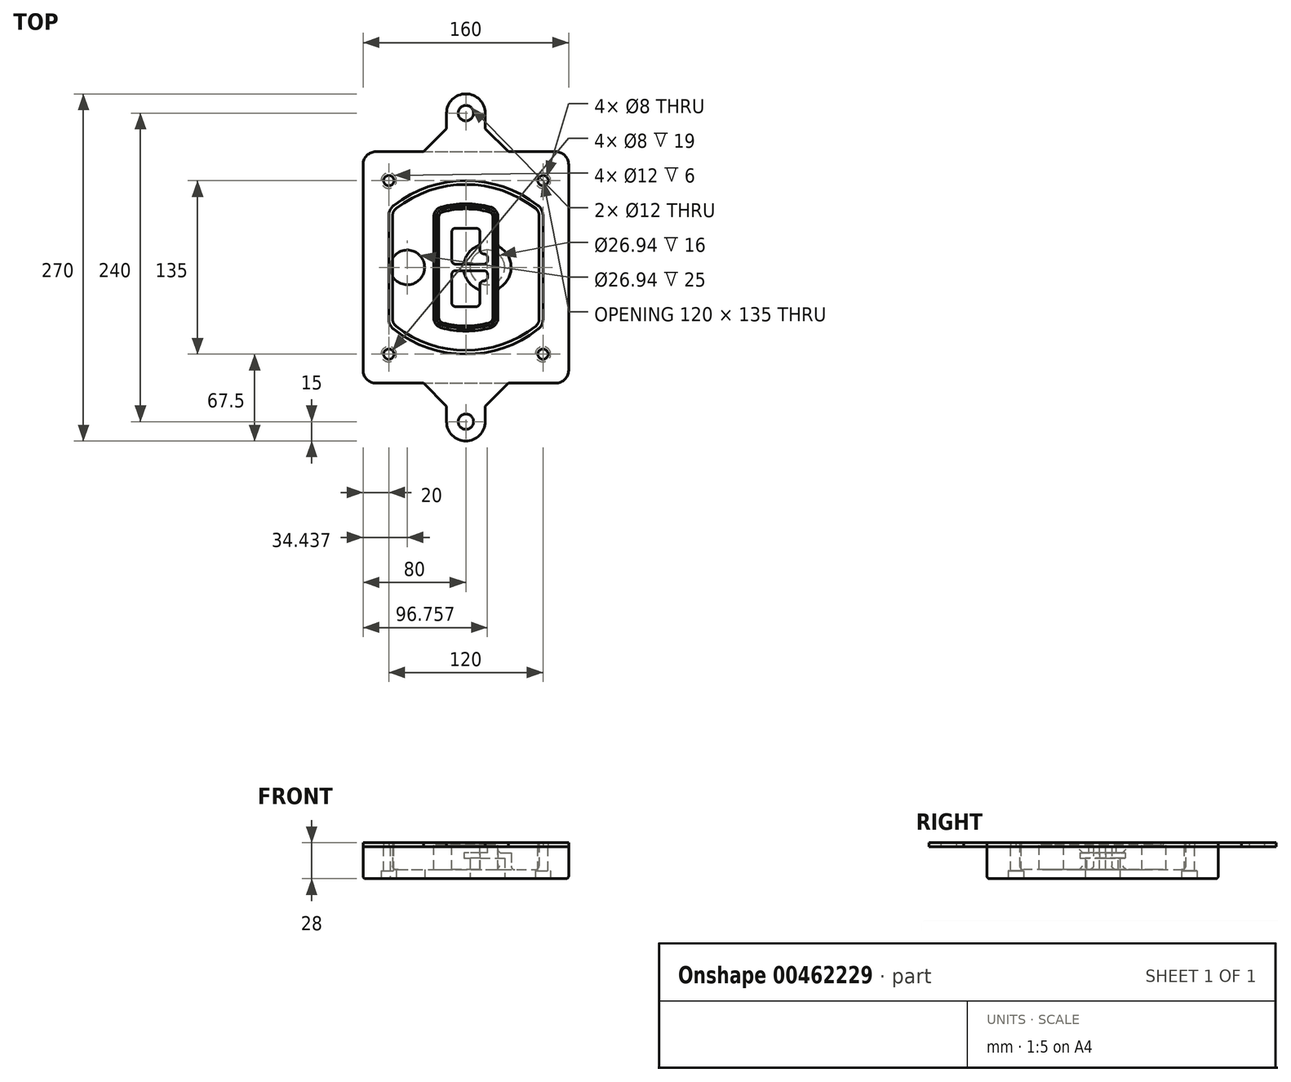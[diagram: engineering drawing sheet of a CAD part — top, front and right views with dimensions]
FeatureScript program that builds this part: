
annotation { "Feature Type Name" : "Feature", "Feature Type Description" : "" }
export const myFeature = defineFeature(function(context is Context, id is Id, definition is map)
    precondition{}
    {
        {
            var Q0;
            Q0=qCreatedBy(makeId("Top.planeOp"),FACE);
            var sketch = newSketch(context, id + "F0", { "sketchPlane" : qUnion([Q0])});
            skPoint(sketch, "E0.rect.middle", {"position": v(0, 0) * mm});
            skLineSegment(sketch, "E1.bottom", {"start": v(-70, -90) * mm, "end": v(70, -90) * mm});
            skLineSegment(sketch, "E1.top", {"start": v(-70, 90) * mm, "end": v(70, 90) * mm});
            skLineSegment(sketch, "E1.left", {"start": v(-80, -80) * mm, "end": v(-80, 80) * mm});
            skLineSegment(sketch, "E1.right", {"start": v(80, -80) * mm, "end": v(80, 80) * mm});
            skLineSegment(sketch, "E2", {"start": v(-80, 90) * mm, "end": v(80, -90) * mm, "construction": true});
            skLineSegment(sketch, "E3", {"start": v(80, 90) * mm, "end": v(-80, -90) * mm, "construction": true});
            skCircle(sketch, "E4", {"center": v(-60, 67.5) * mm, "radius": 4 * mm});
            skCircle(sketch, "E5", {"center": v(60, 67.5) * mm, "radius": 4 * mm});
            skCircle(sketch, "E6", {"center": v(60, -67.5) * mm, "radius": 4 * mm});
            skCircle(sketch, "E7", {"center": v(-60, -67.5) * mm, "radius": 4 * mm});
            skLineSegment(sketch, "E8", {"start": v(-60, 67.5) * mm, "end": v(60, 67.5) * mm, "construction": true});
            skLineSegment(sketch, "E9", {"start": v(60, 67.5) * mm, "end": v(60, -67.5) * mm, "construction": true});
            skLineSegment(sketch, "E10", {"start": v(60, -67.5) * mm, "end": v(-60, -67.5) * mm, "construction": true});
            skLineSegment(sketch, "E11", {"start": v(-60, -67.5) * mm, "end": v(-60, 67.5) * mm, "construction": true});
            skLineSegment(sketch, "E12", {"start": v(-60, 40.3) * mm, "end": v(-60, -40.3) * mm});
            skLineSegment(sketch, "E13", {"start": v(60, 40.3) * mm, "end": v(60, -40.3) * mm});
            skArc(sketch, "E14", {"start": v(56.15, 48.18) * mm, "mid": v(0, 67.5) * mm, "end": v(-56.15, 48.18) * mm});
            skArc(sketch, "E15", {"start": v(-56.15, -48.18) * mm, "mid": v(0, -67.5) * mm, "end": v(56.15, -48.18) * mm});
            skLineSegment(sketch, "E16", {"start": v(-60, 0) * mm, "end": v(60, 0) * mm, "construction": true});
            skPoint(sketch, "E17.visualSharp", {"position": v(-60, -45) * mm});
            skArc(sketch, "E17.filletArc", {"start": v(-60, -40.3) * mm, "mid": v(-58.99, -44.68) * mm, "end": v(-56.15, -48.18) * mm});
            skPoint(sketch, "E18.visualSharp", {"position": v(-60, 45) * mm});
            skArc(sketch, "E18.filletArc", {"start": v(-56.15, 48.18) * mm, "mid": v(-58.99, 44.68) * mm, "end": v(-60, 40.3) * mm});
            skPoint(sketch, "E19.visualSharp", {"position": v(60, 45) * mm});
            skArc(sketch, "E19.filletArc", {"start": v(60, 40.3) * mm, "mid": v(58.99, 44.68) * mm, "end": v(56.15, 48.18) * mm});
            skPoint(sketch, "E20.visualSharp", {"position": v(60, -45) * mm});
            skArc(sketch, "E20.filletArc", {"start": v(56.15, -48.18) * mm, "mid": v(58.99, -44.68) * mm, "end": v(60, -40.3) * mm});
            skPoint(sketch, "E21.visualSharp", {"position": v(-80, 90) * mm});
            skArc(sketch, "E21.filletArc", {"start": v(-70, 90) * mm, "mid": v(-77.07, 87.07) * mm, "end": v(-80, 80) * mm});
            skPoint(sketch, "E22.visualSharp", {"position": v(80, 90) * mm});
            skArc(sketch, "E22.filletArc", {"start": v(80, 80) * mm, "mid": v(77.07, 87.07) * mm, "end": v(70, 90) * mm});
            skPoint(sketch, "E23.visualSharp", {"position": v(80, -90) * mm});
            skArc(sketch, "E23.filletArc", {"start": v(70, -90) * mm, "mid": v(77.07, -87.07) * mm, "end": v(80, -80) * mm});
            skPoint(sketch, "E24.visualSharp", {"position": v(-80, -90) * mm});
            skArc(sketch, "E24.filletArc", {"start": v(-80, -80) * mm, "mid": v(-77.07, -87.07) * mm, "end": v(-70, -90) * mm});
            skArc(sketch, "E25.0", {"start": v(57, 40.3) * mm, "mid": v(56.3, 43.36) * mm, "end": v(54.3, 45.81) * mm});
            skLineSegment(sketch, "E25.1", {"start": v(57, 40.3) * mm, "end": v(57, -40.3) * mm});
            skArc(sketch, "E25.2", {"start": v(54.3, -45.81) * mm, "mid": v(56.3, -43.36) * mm, "end": v(57, -40.3) * mm});
            skArc(sketch, "E25.3", {"start": v(-54.3, -45.81) * mm, "mid": v(0, -64.5) * mm, "end": v(54.3, -45.81) * mm});
            skArc(sketch, "E25.4", {"start": v(-57, -40.3) * mm, "mid": v(-56.3, -43.36) * mm, "end": v(-54.3, -45.81) * mm});
            skArc(sketch, "E25.5", {"start": v(54.3, 45.81) * mm, "mid": v(0, 64.5) * mm, "end": v(-54.3, 45.81) * mm});
            skLineSegment(sketch, "E25.6", {"start": v(-57, 40.3) * mm, "end": v(-57, -40.3) * mm});
            skArc(sketch, "E25.7", {"start": v(-54.3, 45.81) * mm, "mid": v(-56.3, 43.36) * mm, "end": v(-57, 40.3) * mm});
            skArc(sketch, "E26.0", {"start": v(-58.62, 51.33) * mm, "mid": v(-62.58, 46.43) * mm, "end": v(-64, 40.3) * mm});
            skArc(sketch, "E26.1", {"start": v(58.62, 51.33) * mm, "mid": v(0, 71.5) * mm, "end": v(-58.62, 51.33) * mm});
            skArc(sketch, "E26.2", {"start": v(64, 40.3) * mm, "mid": v(62.58, 46.43) * mm, "end": v(58.62, 51.33) * mm});
            skLineSegment(sketch, "E26.3", {"start": v(64, 40.3) * mm, "end": v(64, -40.3) * mm});
            skArc(sketch, "E26.4", {"start": v(58.62, -51.33) * mm, "mid": v(62.58, -46.43) * mm, "end": v(64, -40.3) * mm});
            skLineSegment(sketch, "E26.5", {"start": v(-64, 40.3) * mm, "end": v(-64, -40.3) * mm});
            skArc(sketch, "E26.6", {"start": v(-58.62, -51.33) * mm, "mid": v(0, -71.5) * mm, "end": v(58.62, -51.33) * mm});
            skArc(sketch, "E26.7", {"start": v(-64, -40.3) * mm, "mid": v(-62.58, -46.43) * mm, "end": v(-58.62, -51.33) * mm});
            skSolve(sketch);
        }
        {
            var Q0;
            Q0=makeQuery(id+"F0.imprint","IMPRINT",FACE,{"disambiguationData":[TD([[makeQuery(id+"F0.imprint","IMPRINT",EDGE,{"derivedFrom":sQuery(id+"F0.wireOp",EDGE,"E1.bottom")}),1.0]])]});
            var Q1;
            Q1=makeQuery(id+"F0.imprint","IMPRINT",FACE,{"disambiguationData":[TD([[makeQuery(id+"F0.imprint","IMPRINT",EDGE,{"derivedFrom":sQuery(id+"F0.wireOp",EDGE,"E12")}),1.0]])]});
            var Q2;
            Q2=makeQuery(id+"F0.imprint","IMPRINT",FACE,{"disambiguationData":[TD([[makeQuery(id+"F0.imprint","IMPRINT",EDGE,{"derivedFrom":sQuery(id+"F0.wireOp",EDGE,"E25.0")}),1.0]])]});
            var Q3;
            Q3=makeQuery(id+"F0.imprint","IMPRINT",FACE,{"disambiguationData":[TD([[makeQuery(id+"F0.imprint","IMPRINT",EDGE,{"derivedFrom":sQuery(id+"F0.wireOp",EDGE,"E12")}),-1.0]])]});
            extrude(context, id + "F1", {"entities" : qUnion([Q0, Q1, Q2, Q3]), "oppositeDirection" : true, "depth" : 25 * mm});
        }
        {
            var Q0;
            Q0=makeQuery(id+"F0.imprint","IMPRINT",FACE,{"disambiguationData":[TD([[makeQuery(id+"F0.imprint","IMPRINT",EDGE,{"derivedFrom":sQuery(id+"F0.wireOp",EDGE,"E12")}),1.0]])]});
            extrude(context, id + "F2", {"entities" : qUnion([Q0]), "operationType" : NewBodyOperationType.ADD, "depth" : 3 * mm});
        }
        {
            var Q0;
            Q0=makeQuery(id+"F0.imprint","IMPRINT",FACE,{"disambiguationData":[TD([[makeQuery(id+"F0.imprint","IMPRINT",EDGE,{"derivedFrom":sQuery(id+"F0.wireOp",EDGE,"E25.0")}),1.0]])]});
            extrude(context, id + "F3", {"entities" : qUnion([Q0]), "operationType" : NewBodyOperationType.REMOVE, "oppositeDirection" : true, "depth" : 18 * mm});
        }
        {
            var Q0;
            Q0=makeQuery(id+"F2.opExtrude","CAP_FACE",FACE,{"disambiguationData":[OSD([sQuery(id+"F0.wireOp",EDGE,"E12"),sQuery(id+"F0.wireOp",EDGE,"E13"),sQuery(id+"F0.wireOp",EDGE,"E14"),sQuery(id+"F0.wireOp",EDGE,"E15"),sQuery(id+"F0.wireOp",EDGE,"E17.filletArc"),sQuery(id+"F0.wireOp",EDGE,"E18.filletArc"),sQuery(id+"F0.wireOp",EDGE,"E19.filletArc"),sQuery(id+"F0.wireOp",EDGE,"E20.filletArc"),sQuery(id+"F0.wireOp",EDGE,"E25.0"),sQuery(id+"F0.wireOp",EDGE,"E25.1"),sQuery(id+"F0.wireOp",EDGE,"E25.2"),sQuery(id+"F0.wireOp",EDGE,"E25.3"),sQuery(id+"F0.wireOp",EDGE,"E25.4"),sQuery(id+"F0.wireOp",EDGE,"E25.5"),sQuery(id+"F0.wireOp",EDGE,"E25.6"),sQuery(id+"F0.wireOp",EDGE,"E25.7")])],"isStart":false});
            var sketch = newSketch(context, id + "F4", { "sketchPlane" : qUnion([Q0])});
            skArc(sketch, "E27.0", {"start": v(-19.08, -46.97) * mm, "mid": v(0, -49.5) * mm, "end": v(19.08, -46.97) * mm});
            skArc(sketch, "E28.0", {"start": v(19.08, 46.97) * mm, "mid": v(0, 49.5) * mm, "end": v(-19.08, 46.97) * mm});
            skLineSegment(sketch, "E29", {"start": v(-25, 39.25) * mm, "end": v(-25, -39.25) * mm});
            skLineSegment(sketch, "E30", {"start": v(25, 39.25) * mm, "end": v(25, -39.25) * mm});
            skLineSegment(sketch, "E31", {"start": v(-25, 45.1) * mm, "end": v(25, 45.1) * mm, "construction": true});
            skLineSegment(sketch, "E32", {"start": v(-25, -45.1) * mm, "end": v(25, -45.1) * mm, "construction": true});
            skPoint(sketch, "E33.visualSharp", {"position": v(-25, 45.1) * mm});
            skArc(sketch, "E33.filletArc", {"start": v(-19.08, 46.97) * mm, "mid": v(-23.35, 44.11) * mm, "end": v(-25, 39.25) * mm});
            skPoint(sketch, "E34.visualSharp", {"position": v(25, 45.1) * mm});
            skArc(sketch, "E34.filletArc", {"start": v(25, 39.25) * mm, "mid": v(23.35, 44.11) * mm, "end": v(19.08, 46.97) * mm});
            skPoint(sketch, "E35.visualSharp", {"position": v(25, -45.1) * mm});
            skArc(sketch, "E35.filletArc", {"start": v(19.08, -46.97) * mm, "mid": v(23.35, -44.11) * mm, "end": v(25, -39.25) * mm});
            skPoint(sketch, "E36.visualSharp", {"position": v(-25, -45.1) * mm});
            skArc(sketch, "E36.filletArc", {"start": v(-25, -39.25) * mm, "mid": v(-23.35, -44.11) * mm, "end": v(-19.08, -46.97) * mm});
            skArc(sketch, "E37.0", {"start": v(54.3, 45.81) * mm, "mid": v(0, 64.5) * mm, "end": v(-54.3, 45.81) * mm});
            skArc(sketch, "E37.1", {"start": v(-54.3, 45.81) * mm, "mid": v(-56.3, 43.36) * mm, "end": v(-57, 40.3) * mm});
            skLineSegment(sketch, "E37.2", {"start": v(-57, 40.3) * mm, "end": v(-57, -40.3) * mm});
            skArc(sketch, "E37.3", {"start": v(-57, -40.3) * mm, "mid": v(-56.3, -43.36) * mm, "end": v(-54.3, -45.81) * mm});
            skArc(sketch, "E37.4", {"start": v(-54.3, -45.81) * mm, "mid": v(0, -64.5) * mm, "end": v(54.3, -45.81) * mm});
            skArc(sketch, "E37.5", {"start": v(54.3, -45.81) * mm, "mid": v(56.3, -43.36) * mm, "end": v(57, -40.3) * mm});
            skLineSegment(sketch, "E37.6", {"start": v(57, 40.3) * mm, "end": v(57, -40.3) * mm});
            skArc(sketch, "E37.7", {"start": v(57, 40.3) * mm, "mid": v(56.3, 43.36) * mm, "end": v(54.3, 45.81) * mm});
            skLineSegment(sketch, "E38.0", {"start": v(23, 39.25) * mm, "end": v(23, -39.25) * mm});
            skArc(sketch, "E38.1", {"start": v(18.56, -45.04) * mm, "mid": v(21.76, -42.9) * mm, "end": v(23, -39.25) * mm});
            skArc(sketch, "E38.2", {"start": v(-18.56, -45.04) * mm, "mid": v(0, -47.5) * mm, "end": v(18.56, -45.04) * mm});
            skArc(sketch, "E38.3", {"start": v(-23, -39.25) * mm, "mid": v(-21.76, -42.9) * mm, "end": v(-18.56, -45.04) * mm});
            skLineSegment(sketch, "E38.4", {"start": v(-23, 39.25) * mm, "end": v(-23, -39.25) * mm});
            skArc(sketch, "E38.5", {"start": v(23, 39.25) * mm, "mid": v(21.76, 42.9) * mm, "end": v(18.56, 45.04) * mm});
            skArc(sketch, "E38.6", {"start": v(-18.56, 45.04) * mm, "mid": v(-21.76, 42.9) * mm, "end": v(-23, 39.25) * mm});
            skArc(sketch, "E38.7", {"start": v(18.56, 45.04) * mm, "mid": v(0, 47.5) * mm, "end": v(-18.56, 45.04) * mm});
            skArc(sketch, "E39.0", {"start": v(21, 39.25) * mm, "mid": v(20.18, 41.68) * mm, "end": v(18.04, 43.1) * mm});
            skLineSegment(sketch, "E39.1", {"start": v(21, 39.25) * mm, "end": v(21, -39.25) * mm});
            skArc(sketch, "E39.2", {"start": v(18.04, -43.1) * mm, "mid": v(20.18, -41.68) * mm, "end": v(21, -39.25) * mm});
            skArc(sketch, "E39.3", {"start": v(-18.04, -43.1) * mm, "mid": v(0, -45.5) * mm, "end": v(18.04, -43.1) * mm});
            skArc(sketch, "E39.4", {"start": v(-21, -39.25) * mm, "mid": v(-20.18, -41.68) * mm, "end": v(-18.04, -43.1) * mm});
            skArc(sketch, "E39.5", {"start": v(18.04, 43.1) * mm, "mid": v(0, 45.5) * mm, "end": v(-18.04, 43.1) * mm});
            skLineSegment(sketch, "E39.6", {"start": v(-21, 39.25) * mm, "end": v(-21, -39.25) * mm});
            skArc(sketch, "E39.7", {"start": v(-18.04, 43.1) * mm, "mid": v(-20.18, 41.68) * mm, "end": v(-21, 39.25) * mm});
            skLineSegment(sketch, "E40", {"start": v(-25, 0) * mm, "end": v(25, 0) * mm, "construction": true});
            skLineSegment(sketch, "E41", {"start": v(-11, 5.5) * mm, "end": v(-11, 27.5) * mm});
            skLineSegment(sketch, "E42", {"start": v(-8, 30.5) * mm, "end": v(8, 30.5) * mm});
            skLineSegment(sketch, "E43", {"start": v(11, 27.5) * mm, "end": v(11, 13.5) * mm});
            skLineSegment(sketch, "E44", {"start": v(14, 10.5) * mm, "end": v(14, 10.5) * mm});
            skLineSegment(sketch, "E45", {"start": v(17, 7.5) * mm, "end": v(17, 5.5) * mm});
            skLineSegment(sketch, "E46", {"start": v(14, 2.5) * mm, "end": v(-8, 2.5) * mm});
            skPoint(sketch, "E47.visualSharp", {"position": v(-11, 30.5) * mm});
            skArc(sketch, "E47.filletArc", {"start": v(-8, 30.5) * mm, "mid": v(-10.12, 29.62) * mm, "end": v(-11, 27.5) * mm});
            skPoint(sketch, "E48.visualSharp", {"position": v(11, 30.5) * mm});
            skArc(sketch, "E48.filletArc", {"start": v(11, 27.5) * mm, "mid": v(10.12, 29.62) * mm, "end": v(8, 30.5) * mm});
            skPoint(sketch, "E49.visualSharp", {"position": v(11, 10.5) * mm});
            skArc(sketch, "E49.filletArc", {"start": v(11, 13.5) * mm, "mid": v(11.88, 11.38) * mm, "end": v(14, 10.5) * mm});
            skPoint(sketch, "E50.visualSharp", {"position": v(17, 10.5) * mm});
            skArc(sketch, "E50.filletArc", {"start": v(17, 7.5) * mm, "mid": v(16.12, 9.62) * mm, "end": v(14, 10.5) * mm});
            skPoint(sketch, "E51.visualSharp", {"position": v(17, 2.5) * mm});
            skArc(sketch, "E51.filletArc", {"start": v(14, 2.5) * mm, "mid": v(16.12, 3.38) * mm, "end": v(17, 5.5) * mm});
            skPoint(sketch, "E52.visualSharp", {"position": v(-11, 2.5) * mm});
            skArc(sketch, "E52.filletArc", {"start": v(-11, 5.5) * mm, "mid": v(-10.12, 3.38) * mm, "end": v(-8, 2.5) * mm});
            skLineSegment(sketch, "E53.0.MirrorCS", {"start": v(14, -2.5) * mm, "end": v(-8, -2.5) * mm});
            skArc(sketch, "E54.0.MirrorCS", {"start": v(-11, -5.5) * mm, "mid": v(-10.12, -3.38) * mm, "end": v(-8, -2.5) * mm});
            skLineSegment(sketch, "E55.0.MirrorCS", {"start": v(-11, -5.5) * mm, "end": v(-11, -27.5) * mm});
            skArc(sketch, "E56.0.MirrorCS", {"start": v(-8, -30.5) * mm, "mid": v(-10.12, -29.62) * mm, "end": v(-11, -27.5) * mm});
            skLineSegment(sketch, "E57.0.MirrorCS", {"start": v(-8, -30.5) * mm, "end": v(8, -30.5) * mm});
            skArc(sketch, "E58.0.MirrorCS", {"start": v(11, -27.5) * mm, "mid": v(10.12, -29.62) * mm, "end": v(8, -30.5) * mm});
            skLineSegment(sketch, "E59.0.MirrorCS", {"start": v(11, -27.5) * mm, "end": v(11, -13.5) * mm});
            skArc(sketch, "E60.0.MirrorCS", {"start": v(11, -13.5) * mm, "mid": v(11.88, -11.38) * mm, "end": v(14, -10.5) * mm});
            skArc(sketch, "E61.0.MirrorCS", {"start": v(17, -7.5) * mm, "mid": v(16.12, -9.62) * mm, "end": v(14, -10.5) * mm});
            skLineSegment(sketch, "E62.0.MirrorCS", {"start": v(17, -7.5) * mm, "end": v(17, -5.5) * mm});
            skArc(sketch, "E63.0.MirrorCS", {"start": v(14, -2.5) * mm, "mid": v(16.12, -3.38) * mm, "end": v(17, -5.5) * mm});
            skSolve(sketch);
        }
        {
            var Q0;
            Q0=makeQuery(id+"F4.imprint","IMPRINT",FACE,{"disambiguationData":[TD([[makeQuery(id+"F4.imprint","IMPRINT",EDGE,{"derivedFrom":sQuery(id+"F4.wireOp",EDGE,"E27.0")}),1.0]])]});
            var Q1;
            Q1=makeQuery(id+"F4.imprint","IMPRINT",FACE,{"disambiguationData":[TD([[makeQuery(id+"F4.imprint","IMPRINT",EDGE,{"derivedFrom":sQuery(id+"F4.wireOp",EDGE,"E38.0")}),-1.0]])]});
            var Q2;
            Q2=makeQuery(id+"F4.imprint","IMPRINT",FACE,{"disambiguationData":[TD([[makeQuery(id+"F4.imprint","IMPRINT",EDGE,{"derivedFrom":sQuery(id+"F4.wireOp",EDGE,"E39.0")}),1.0]])]});
            extrude(context, id + "F5", {"entities" : qUnion([Q0, Q1, Q2]), "operationType" : NewBodyOperationType.ADD, "endBound" : BoundingType.UP_TO_NEXT, "oppositeDirection" : true, "depth" : 25 * mm});
        }
        {
            var Q0;
            Q0=makeQuery(id+"F4.imprint","IMPRINT",FACE,{"disambiguationData":[TD([[makeQuery(id+"F4.imprint","IMPRINT",EDGE,{"derivedFrom":sQuery(id+"F4.wireOp",EDGE,"E38.0")}),-1.0]])]});
            extrude(context, id + "F6", {"entities" : qUnion([Q0]), "operationType" : NewBodyOperationType.REMOVE, "oppositeDirection" : true, "depth" : 2 * mm});
        }
        {
            var Q0;
            Q0=makeQuery(id+"F1.opExtrude","CAP_FACE",FACE,{"disambiguationData":[OSD([sQuery(id+"F0.wireOp",EDGE,"E1.bottom"),sQuery(id+"F0.wireOp",EDGE,"E1.top"),sQuery(id+"F0.wireOp",EDGE,"E1.left"),sQuery(id+"F0.wireOp",EDGE,"E1.right"),sQuery(id+"F0.wireOp",EDGE,"E4"),sQuery(id+"F0.wireOp",EDGE,"E5"),sQuery(id+"F0.wireOp",EDGE,"E6"),sQuery(id+"F0.wireOp",EDGE,"E7"),sQuery(id+"F0.wireOp",EDGE,"E21.filletArc"),sQuery(id+"F0.wireOp",EDGE,"E22.filletArc"),sQuery(id+"F0.wireOp",EDGE,"E23.filletArc"),sQuery(id+"F0.wireOp",EDGE,"E24.filletArc")])],"isStart":false});
            var sketch = newSketch(context, id + "F7", { "sketchPlane" : qUnion([Q0])});
            skCircle(sketch, "E64", {"center": v(16.76, 0) * mm, "radius": 13.47 * mm});
            skCircle(sketch, "E65", {"center": v(-45.56, 0) * mm, "radius": 13.47 * mm});
            skLineSegment(sketch, "E66", {"start": v(80, 0) * mm, "end": v(-80, 0) * mm});
            skCircle(sketch, "E67", {"center": v(16.76, 0) * mm, "radius": 18.47 * mm});
            skCircle(sketch, "E68", {"center": v(60, -67.5) * mm, "radius": 6 * mm});
            skCircle(sketch, "E69", {"center": v(-60, -67.5) * mm, "radius": 6 * mm});
            skCircle(sketch, "E70", {"center": v(-60, 67.5) * mm, "radius": 6 * mm});
            skCircle(sketch, "E71", {"center": v(60, 67.5) * mm, "radius": 6 * mm});
            skSolve(sketch);
        }
        {
            var Q0;
            {var subQ1=sQuery(id+"F7.wireOp",EDGE,"E66");var subQ4=sQuery(id+"F7.wireOp",EDGE,"E64");var subQ6=makeQuery(id+"F7.imprint","INTERSECT",VERTEX,{"disambiguationData":[OD(0.0)],"derivedFrom":[subQ4,subQ1]});Q0=makeQuery(id+"F7.imprint","IMPRINT",FACE,{"disambiguationData":[TD([[makeQuery(id+"F7.imprint","IMPRINT",EDGE,{"disambiguationData":[TD([[subQ6,-1.0]])],"derivedFrom":subQ4}),-1.0]])]});}
            var Q1;
            {var subQ0=sQuery(id+"F7.wireOp",EDGE,"E66");var subQ1=sQuery(id+"F7.wireOp",EDGE,"E64");var subQ3=makeQuery(id+"F7.imprint","INTERSECT",VERTEX,{"disambiguationData":[OD(0.0)],"derivedFrom":[subQ1,subQ0]});Q1=makeQuery(id+"F7.imprint","IMPRINT",FACE,{"disambiguationData":[TD([[makeQuery(id+"F7.imprint","IMPRINT",EDGE,{"disambiguationData":[TD([[subQ3,-1.0]])],"derivedFrom":subQ1}),1.0]])]});}
            var Q2;
            {var subQ0=sQuery(id+"F7.wireOp",EDGE,"E66");var subQ1=sQuery(id+"F7.wireOp",EDGE,"E64");var subQ3=makeQuery(id+"F7.imprint","INTERSECT",VERTEX,{"disambiguationData":[OD(0.0)],"derivedFrom":[subQ1,subQ0]});Q2=makeQuery(id+"F7.imprint","IMPRINT",FACE,{"disambiguationData":[TD([[makeQuery(id+"F7.imprint","IMPRINT",EDGE,{"disambiguationData":[TD([[subQ3,1.0]])],"derivedFrom":subQ1}),1.0]])]});}
            var Q3;
            {var subQ1=sQuery(id+"F7.wireOp",EDGE,"E66");var subQ4=sQuery(id+"F7.wireOp",EDGE,"E64");var subQ6=makeQuery(id+"F7.imprint","INTERSECT",VERTEX,{"disambiguationData":[OD(0.0)],"derivedFrom":[subQ4,subQ1]});Q3=makeQuery(id+"F7.imprint","IMPRINT",FACE,{"disambiguationData":[TD([[makeQuery(id+"F7.imprint","IMPRINT",EDGE,{"disambiguationData":[TD([[subQ6,1.0]])],"derivedFrom":subQ4}),-1.0]])]});}
            extrude(context, id + "F8", {"entities" : qUnion([Q0, Q1, Q2, Q3]), "operationType" : NewBodyOperationType.ADD, "oppositeDirection" : true, "depth" : 20 * mm});
        }
        {
            var Q0;
            {var subQ0=sQuery(id+"F7.wireOp",EDGE,"E66");var subQ1=sQuery(id+"F7.wireOp",EDGE,"E64");var subQ3=makeQuery(id+"F7.imprint","INTERSECT",VERTEX,{"disambiguationData":[OD(0.0)],"derivedFrom":[subQ1,subQ0]});Q0=makeQuery(id+"F7.imprint","IMPRINT",FACE,{"disambiguationData":[TD([[makeQuery(id+"F7.imprint","IMPRINT",EDGE,{"disambiguationData":[TD([[subQ3,-1.0]])],"derivedFrom":subQ1}),1.0]])]});}
            var Q1;
            {var subQ0=sQuery(id+"F7.wireOp",EDGE,"E66");var subQ1=sQuery(id+"F7.wireOp",EDGE,"E64");var subQ3=makeQuery(id+"F7.imprint","INTERSECT",VERTEX,{"disambiguationData":[OD(0.0)],"derivedFrom":[subQ1,subQ0]});Q1=makeQuery(id+"F7.imprint","IMPRINT",FACE,{"disambiguationData":[TD([[makeQuery(id+"F7.imprint","IMPRINT",EDGE,{"disambiguationData":[TD([[subQ3,1.0]])],"derivedFrom":subQ1}),1.0]])]});}
            extrude(context, id + "F9", {"entities" : qUnion([Q0, Q1]), "operationType" : NewBodyOperationType.REMOVE, "oppositeDirection" : true, "depth" : 16 * mm});
        }
        {
            var Q0;
            {var subQ0=sQuery(id+"F7.wireOp",EDGE,"E66");var subQ1=sQuery(id+"F7.wireOp",EDGE,"E65");var subQ3=makeQuery(id+"F7.imprint","INTERSECT",VERTEX,{"disambiguationData":[OD(0.0)],"derivedFrom":[subQ1,subQ0]});Q0=makeQuery(id+"F7.imprint","IMPRINT",FACE,{"disambiguationData":[TD([[makeQuery(id+"F7.imprint","IMPRINT",EDGE,{"disambiguationData":[TD([[subQ3,-1.0]])],"derivedFrom":subQ1}),1.0]])]});}
            var Q1;
            {var subQ0=sQuery(id+"F7.wireOp",EDGE,"E66");var subQ1=sQuery(id+"F7.wireOp",EDGE,"E65");var subQ3=makeQuery(id+"F7.imprint","INTERSECT",VERTEX,{"disambiguationData":[OD(0.0)],"derivedFrom":[subQ1,subQ0]});Q1=makeQuery(id+"F7.imprint","IMPRINT",FACE,{"disambiguationData":[TD([[makeQuery(id+"F7.imprint","IMPRINT",EDGE,{"disambiguationData":[TD([[subQ3,1.0]])],"derivedFrom":subQ1}),1.0]])]});}
            extrude(context, id + "F10", {"entities" : qUnion([Q0, Q1]), "operationType" : NewBodyOperationType.REMOVE, "oppositeDirection" : true, "depth" : 25 * mm});
        }
        {
            var Q0;
            Q0=makeQuery(id+"F7.imprint","IMPRINT",FACE,{"disambiguationData":[TD([[makeQuery(id+"F7.imprint","IMPRINT",EDGE,{"derivedFrom":sQuery(id+"F7.wireOp",EDGE,"E68")}),1.0]])]});
            var Q1;
            Q1=makeQuery(id+"F7.imprint","IMPRINT",FACE,{"disambiguationData":[TD([[makeQuery(id+"F7.imprint","IMPRINT",EDGE,{"derivedFrom":makeQuery(id+"F1.opExtrude","CAP_EDGE",EDGE,{"disambiguationData":[OSD([sQuery(id+"F0.wireOp",EDGE,"E5")])],"isStart":false})}),-1.0]])]});
            var Q2;
            Q2=makeQuery(id+"F7.imprint","IMPRINT",FACE,{"disambiguationData":[TD([[makeQuery(id+"F7.imprint","IMPRINT",EDGE,{"derivedFrom":sQuery(id+"F7.wireOp",EDGE,"E69")}),1.0]])]});
            var Q3;
            Q3=makeQuery(id+"F7.imprint","IMPRINT",FACE,{"disambiguationData":[TD([[makeQuery(id+"F7.imprint","IMPRINT",EDGE,{"derivedFrom":makeQuery(id+"F1.opExtrude","CAP_EDGE",EDGE,{"disambiguationData":[OSD([sQuery(id+"F0.wireOp",EDGE,"E4")])],"isStart":false})}),-1.0]])]});
            var Q4;
            Q4=makeQuery(id+"F7.imprint","IMPRINT",FACE,{"disambiguationData":[TD([[makeQuery(id+"F7.imprint","IMPRINT",EDGE,{"derivedFrom":sQuery(id+"F7.wireOp",EDGE,"E70")}),1.0]])]});
            var Q5;
            Q5=makeQuery(id+"F7.imprint","IMPRINT",FACE,{"disambiguationData":[TD([[makeQuery(id+"F7.imprint","IMPRINT",EDGE,{"derivedFrom":makeQuery(id+"F1.opExtrude","CAP_EDGE",EDGE,{"disambiguationData":[OSD([sQuery(id+"F0.wireOp",EDGE,"E7")])],"isStart":false})}),-1.0]])]});
            var Q6;
            Q6=makeQuery(id+"F7.imprint","IMPRINT",FACE,{"disambiguationData":[TD([[makeQuery(id+"F7.imprint","IMPRINT",EDGE,{"derivedFrom":sQuery(id+"F7.wireOp",EDGE,"E71")}),1.0]])]});
            var Q7;
            Q7=makeQuery(id+"F7.imprint","IMPRINT",FACE,{"disambiguationData":[TD([[makeQuery(id+"F7.imprint","IMPRINT",EDGE,{"derivedFrom":makeQuery(id+"F1.opExtrude","CAP_EDGE",EDGE,{"disambiguationData":[OSD([sQuery(id+"F0.wireOp",EDGE,"E6")])],"isStart":false})}),-1.0]])]});
            extrude(context, id + "F11", {"entities" : qUnion([Q0, Q1, Q2, Q3, Q4, Q5, Q6, Q7]), "operationType" : NewBodyOperationType.REMOVE, "oppositeDirection" : true, "depth" : 6 * mm});
        }
        {
            var Q0;
            Q0=makeQuery(id+"F9.boolean.opBoolean","COPY",FACE,{"derivedFrom":makeQuery(id+"F9.opExtrude","CAP_FACE",FACE,{"disambiguationData":[OSD([sQuery(id+"F7.wireOp",EDGE,"E64")])],"isStart":false})});
            var sketch = newSketch(context, id + "F12", { "sketchPlane" : qUnion([Q0])});
            skArc(sketch, "E72.0", {"start": v(11, 17.55) * mm, "mid": v(2.57, 11.82) * mm, "end": v(-1.54, 2.5) * mm});
            skArc(sketch, "E72.1", {"start": v(-1.54, -2.5) * mm, "mid": v(2.57, -11.82) * mm, "end": v(11, -17.55) * mm});
            skLineSegment(sketch, "E73", {"start": v(-1.54, -2.5) * mm, "end": v(14, -2.5) * mm});
            skLineSegment(sketch, "E74.0", {"start": v(14, 2.5) * mm, "end": v(-1.54, 2.5) * mm});
            skArc(sketch, "E74.1", {"start": v(14, 2.5) * mm, "mid": v(16.12, 3.38) * mm, "end": v(17, 5.5) * mm});
            skLineSegment(sketch, "E74.2", {"start": v(17, 7.5) * mm, "end": v(17, 5.5) * mm});
            skArc(sketch, "E74.3", {"start": v(17, 7.5) * mm, "mid": v(16.12, 9.62) * mm, "end": v(14, 10.5) * mm});
            skArc(sketch, "E74.4", {"start": v(11, 13.5) * mm, "mid": v(11.88, 11.38) * mm, "end": v(14, 10.5) * mm});
            skLineSegment(sketch, "E74.5", {"start": v(11, 17.55) * mm, "end": v(11, 13.5) * mm});
            skLineSegment(sketch, "E74.7", {"start": v(14, -2.5) * mm, "end": v(-1.54, -2.5) * mm});
            skArc(sketch, "E74.8", {"start": v(14, -2.5) * mm, "mid": v(16.12, -3.38) * mm, "end": v(17, -5.5) * mm});
            skLineSegment(sketch, "E74.9", {"start": v(17, -7.5) * mm, "end": v(17, -5.5) * mm});
            skArc(sketch, "E74.10", {"start": v(17, -7.5) * mm, "mid": v(16.12, -9.62) * mm, "end": v(14, -10.5) * mm});
            skArc(sketch, "E74.11", {"start": v(11, -13.5) * mm, "mid": v(11.88, -11.38) * mm, "end": v(14, -10.5) * mm});
            skLineSegment(sketch, "E74.12", {"start": v(11, -17.55) * mm, "end": v(11, -13.5) * mm});
            skPoint(sketch, "E75.orphan", {"position": v(11, -27.5) * mm});
            skPoint(sketch, "E76.orphan", {"position": v(-8, -2.5) * mm});
            skPoint(sketch, "E77.orphan", {"position": v(-8, 2.5) * mm});
            skPoint(sketch, "E78.orphan", {"position": v(11, 27.5) * mm});
            skSolve(sketch);
        }
        {
            var Q0;
            {var subQ7=sQuery(id+"F12.wireOp",EDGE,"E72.0");var subQ14=sQuery(id+"F12.wireOp",EDGE,"E72.1");var subQ16=sQuery(id+"F12.wireOp",EDGE,"E74.1");var subQ18=sQuery(id+"F12.wireOp",EDGE,"E74.8");Q0=qUnion([makeQuery(id+"F12.imprint","IMPRINT",FACE,{"disambiguationData":[TD([[makeQuery(id+"F12.imprint","IMPRINT",EDGE,{"derivedFrom":subQ7}),1.0]])]}),makeQuery(id+"F12.imprint","IMPRINT",FACE,{"disambiguationData":[TD([[makeQuery(id+"F12.imprint","IMPRINT",EDGE,{"derivedFrom":subQ14}),1.0]])]}),makeQuery(id+"F12.imprint","IMPRINT",FACE,{"disambiguationData":[TD([[makeQuery(id+"F12.imprint","IMPRINT",EDGE,{"derivedFrom":subQ16}),1.0]])]}),makeQuery(id+"F12.imprint","IMPRINT",FACE,{"disambiguationData":[TD([[makeQuery(id+"F12.imprint","IMPRINT",EDGE,{"derivedFrom":subQ18}),-1.0]])]})]);}
            var Q1;
            Q1=makeQuery(id+"F5.boolean.opBoolean","SPLIT",FACE,{"disambiguationData":[TD([makeQuery(id+"F5.opExtrude","SWEPT_FACE",FACE,{"disambiguationData":[OSD([sQuery(id+"F4.wireOp",EDGE,"E41")])]})])],"derivedFrom":makeQuery(id+"F3.boolean.opBoolean","COPY",FACE,{"derivedFrom":makeQuery(id+"F3.opExtrude","CAP_FACE",FACE,{"disambiguationData":[OSD([sQuery(id+"F0.wireOp",EDGE,"E25.0"),sQuery(id+"F0.wireOp",EDGE,"E25.1"),sQuery(id+"F0.wireOp",EDGE,"E25.2"),sQuery(id+"F0.wireOp",EDGE,"E25.3"),sQuery(id+"F0.wireOp",EDGE,"E25.4"),sQuery(id+"F0.wireOp",EDGE,"E25.5"),sQuery(id+"F0.wireOp",EDGE,"E25.6"),sQuery(id+"F0.wireOp",EDGE,"E25.7")])],"isStart":false})})});
            extrude(context, id + "F13", {"entities" : qUnion([Q0]), "operationType" : NewBodyOperationType.REMOVE, "endBound" : BoundingType.UP_TO_SURFACE, "endBoundEntityFace" : qUnion([Q1]), "depth" : 25 * mm});
        }
        {
            var Q0;
            Q0=makeQuery(id+"F3.boolean.opBoolean","COPY",EDGE,{"derivedFrom":makeQuery(id+"F3.opExtrude","CAP_EDGE",EDGE,{"disambiguationData":[OSD([sQuery(id+"F0.wireOp",EDGE,"E25.6")])],"isStart":false})});
            var Q1;
            Q1=makeQuery(id+"F8.boolean.opBoolean","INTERSECT",EDGE,{"derivedFrom":[makeQuery(id+"F5.opExtrude","SWEPT_FACE",FACE,{"disambiguationData":[OSD([sQuery(id+"F4.wireOp",EDGE,"E30")])]}),makeQuery(id+"F8.opExtrude","CAP_FACE",FACE,{"disambiguationData":[OSD([sQuery(id+"F7.wireOp",EDGE,"E67")])],"isStart":false})]});
            var Q2;
            Q2=makeQuery(id+"F8.boolean.opBoolean","INTERSECT",EDGE,{"disambiguationData":[OD(1.0)],"derivedFrom":[makeQuery(id+"F5.opExtrude","SWEPT_FACE",FACE,{"disambiguationData":[OSD([sQuery(id+"F4.wireOp",EDGE,"E30")])]}),makeQuery(id+"F8.opExtrude","SWEPT_FACE",FACE,{"disambiguationData":[OSD([sQuery(id+"F7.wireOp",EDGE,"E67")])]})]});
            var Q3;
            {var subQ0=sQuery(id+"F4.wireOp",EDGE,"E30");Q3=makeQuery(id+"F8.boolean.opBoolean","SPLIT",EDGE,{"disambiguationData":[TD([makeQuery(id+"F5.opExtrude","SWEPT_FACE",FACE,{"disambiguationData":[OSD([sQuery(id+"F4.wireOp",EDGE,"E35.filletArc")])]})])],"derivedFrom":makeQuery(id+"F5.opExtrude","CAP_EDGE",EDGE,{"disambiguationData":[OSD([subQ0])],"isStart":false})});}
            var Q4;
            {var subQ0=sQuery(id+"F0.wireOp",EDGE,"E25.7");var subQ1=sQuery(id+"F0.wireOp",EDGE,"E25.1");var subQ2=sQuery(id+"F0.wireOp",EDGE,"E25.6");var subQ3=sQuery(id+"F0.wireOp",EDGE,"E25.5");var subQ4=sQuery(id+"F0.wireOp",EDGE,"E25.4");var subQ5=sQuery(id+"F0.wireOp",EDGE,"E25.0");var subQ6=sQuery(id+"F0.wireOp",EDGE,"E25.2");var subQ7=sQuery(id+"F0.wireOp",EDGE,"E25.3");Q4=makeQuery(id+"F8.boolean.opBoolean","INTERSECT",EDGE,{"derivedFrom":[makeQuery(id+"F5.boolean.opBoolean","SPLIT",FACE,{"disambiguationData":[TD([makeQuery(id+"F2.opExtrude","SWEPT_FACE",FACE,{"disambiguationData":[OSD([subQ5])]})])],"derivedFrom":makeQuery(id+"F3.boolean.opBoolean","COPY",FACE,{"derivedFrom":makeQuery(id+"F3.opExtrude","CAP_FACE",FACE,{"disambiguationData":[OSD([subQ5,subQ1,subQ6,subQ7,subQ4,subQ3,subQ2,subQ0])],"isStart":false})})}),makeQuery(id+"F8.opExtrude","SWEPT_FACE",FACE,{"disambiguationData":[OSD([sQuery(id+"F7.wireOp",EDGE,"E67")])]})]});}
            var Q5;
            Q5=makeQuery(id+"F8.boolean.opBoolean","INTERSECT",EDGE,{"disambiguationData":[OD(0.0)],"derivedFrom":[makeQuery(id+"F5.opExtrude","SWEPT_FACE",FACE,{"disambiguationData":[OSD([sQuery(id+"F4.wireOp",EDGE,"E30")])]}),makeQuery(id+"F8.opExtrude","SWEPT_FACE",FACE,{"disambiguationData":[OSD([sQuery(id+"F7.wireOp",EDGE,"E67")])]})]});
            fillet(context, id + "F14", {"entities" : qUnion([Q0, Q1, Q2, Q3, Q4, Q5]), "radius" : 3 * mm, "tangentPropagation" : true, "allowEdgeOverflow" : false});
        }
        {
            var Q0;
            Q0=makeQuery(id+"F1.opExtrude","CAP_EDGE",EDGE,{"disambiguationData":[OSD([sQuery(id+"F0.wireOp",EDGE,"E1.bottom")])],"isStart":false});
            fillet(context, id + "F15", {"entities" : qUnion([Q0]), "radius" : 2 * mm, "tangentPropagation" : true, "allowEdgeOverflow" : false});
        }
        {
            var Q0;
            {var subQ0=sQuery(id+"F0.wireOp",EDGE,"E21.filletArc");var subQ1=sQuery(id+"F0.wireOp",EDGE,"E7");var subQ2=sQuery(id+"F0.wireOp",EDGE,"E6");var subQ3=sQuery(id+"F0.wireOp",EDGE,"E5");var subQ4=sQuery(id+"F0.wireOp",EDGE,"E4");var subQ5=sQuery(id+"F0.wireOp",EDGE,"E22.filletArc");var subQ6=sQuery(id+"F0.wireOp",EDGE,"E1.bottom");var subQ7=sQuery(id+"F0.wireOp",EDGE,"E1.right");var subQ8=sQuery(id+"F0.wireOp",EDGE,"E1.top");var subQ9=sQuery(id+"F0.wireOp",EDGE,"E1.left");var subQ10=sQuery(id+"F0.wireOp",EDGE,"E23.filletArc");var subQ11=sQuery(id+"F0.wireOp",EDGE,"E24.filletArc");Q0=makeQuery(id+"F2.boolean.opBoolean","SPLIT",FACE,{"disambiguationData":[TD([makeQuery(id+"F1.opExtrude","SWEPT_FACE",FACE,{"disambiguationData":[OSD([subQ6])]})])],"derivedFrom":makeQuery(id+"F1.opExtrude","CAP_FACE",FACE,{"disambiguationData":[OSD([subQ6,subQ8,subQ9,subQ7,subQ4,subQ3,subQ2,subQ1,subQ0,subQ5,subQ10,subQ11])],"isStart":true})});}
            var sketch = newSketch(context, id + "F16", { "sketchPlane" : qUnion([Q0])});
            skLineSegment(sketch, "E79.0", {"start": v(-70, 90) * mm, "end": v(70, 90) * mm});
            skArc(sketch, "E80.0", {"start": v(-70, 90) * mm, "mid": v(-77.07, 87.07) * mm, "end": v(-80, 80) * mm});
            skLineSegment(sketch, "E81.0", {"start": v(-80, -80) * mm, "end": v(-80, 80) * mm});
            skArc(sketch, "E82.0", {"start": v(80, 80) * mm, "mid": v(77.07, 87.07) * mm, "end": v(70, 90) * mm});
            skLineSegment(sketch, "E83.0", {"start": v(80, -80) * mm, "end": v(80, 80) * mm});
            skArc(sketch, "E84.0", {"start": v(70, -90) * mm, "mid": v(77.07, -87.07) * mm, "end": v(80, -80) * mm});
            skLineSegment(sketch, "E85.0", {"start": v(-70, -90) * mm, "end": v(70, -90) * mm});
            skCircle(sketch, "E86.0", {"center": v(-60, 67.5) * mm, "radius": 4 * mm});
            skCircle(sketch, "E87.0", {"center": v(-60, -67.5) * mm, "radius": 4 * mm});
            skCircle(sketch, "E88.0", {"center": v(60, -67.5) * mm, "radius": 4 * mm});
            skArc(sketch, "E89.0", {"start": v(-80, -80) * mm, "mid": v(-77.07, -87.07) * mm, "end": v(-70, -90) * mm});
            skArc(sketch, "E90.0", {"start": v(56.15, 48.18) * mm, "mid": v(0, 67.5) * mm, "end": v(-56.15, 48.18) * mm});
            skArc(sketch, "E91.0", {"start": v(-56.15, 48.18) * mm, "mid": v(-58.99, 44.68) * mm, "end": v(-60, 40.3) * mm});
            skLineSegment(sketch, "E92.0", {"start": v(-60, 40.3) * mm, "end": v(-60, -40.3) * mm});
            skArc(sketch, "E93.0", {"start": v(-60, -40.3) * mm, "mid": v(-58.99, -44.68) * mm, "end": v(-56.15, -48.18) * mm});
            skArc(sketch, "E94.0", {"start": v(-56.15, -48.18) * mm, "mid": v(0, -67.5) * mm, "end": v(56.15, -48.18) * mm});
            skArc(sketch, "E95.0", {"start": v(56.15, -48.18) * mm, "mid": v(58.99, -44.68) * mm, "end": v(60, -40.3) * mm});
            skLineSegment(sketch, "E96.0", {"start": v(60, 40.3) * mm, "end": v(60, -40.3) * mm});
            skCircle(sketch, "E97.0", {"center": v(60, 67.5) * mm, "radius": 4 * mm});
            skArc(sketch, "E98.0", {"start": v(60, 40.3) * mm, "mid": v(58.99, 44.68) * mm, "end": v(56.15, 48.18) * mm});
            skLineSegment(sketch, "E99", {"start": v(0, 90) * mm, "end": v(0, 120) * mm, "construction": true});
            skPoint(sketch, "E99.endSnap0", {"position": v(0, 90) * mm});
            skCircle(sketch, "E100", {"center": v(0, 120) * mm, "radius": 6 * mm});
            skArc(sketch, "E101", {"start": v(-15, 120) * mm, "mid": v(0, 135) * mm, "end": v(15, 120) * mm});
            skLineSegment(sketch, "E102", {"start": v(-15, 120) * mm, "end": v(-15, 108) * mm});
            skLineSegment(sketch, "E103", {"start": v(-15, 108) * mm, "end": v(-33, 90) * mm});
            skLineSegment(sketch, "E104.MirrorCS", {"start": v(15, 120) * mm, "end": v(15, 108) * mm});
            skLineSegment(sketch, "E105.MirrorCS", {"start": v(15, 108) * mm, "end": v(33, 90) * mm});
            skLineSegment(sketch, "E106", {"start": v(-80, 0) * mm, "end": v(80, 0) * mm, "construction": true});
            skLineSegment(sketch, "E107.MirrorCS", {"start": v(-15, -108) * mm, "end": v(-33, -90) * mm});
            skLineSegment(sketch, "E108.MirrorCS", {"start": v(-15, -120) * mm, "end": v(-15, -108) * mm});
            skArc(sketch, "E109.MirrorCS", {"start": v(-15, -120) * mm, "mid": v(0, -135) * mm, "end": v(15, -120) * mm});
            skLineSegment(sketch, "E110.MirrorCS", {"start": v(15, -120) * mm, "end": v(15, -108) * mm});
            skLineSegment(sketch, "E111.MirrorCS", {"start": v(15, -108) * mm, "end": v(33, -90) * mm});
            skCircle(sketch, "E112.MirrorC", {"center": v(0, -120) * mm, "radius": 6 * mm});
            skSolve(sketch);
        }
        {
            var Q0;
            Q0=qSketchRegion(id+"F16",true);
            var Q1;
            Q1=makeQuery(id+"F2.opExtrude","CAP_FACE",FACE,{"disambiguationData":[OSD([sQuery(id+"F0.wireOp",EDGE,"E12"),sQuery(id+"F0.wireOp",EDGE,"E13"),sQuery(id+"F0.wireOp",EDGE,"E14"),sQuery(id+"F0.wireOp",EDGE,"E15"),sQuery(id+"F0.wireOp",EDGE,"E17.filletArc"),sQuery(id+"F0.wireOp",EDGE,"E18.filletArc"),sQuery(id+"F0.wireOp",EDGE,"E19.filletArc"),sQuery(id+"F0.wireOp",EDGE,"E20.filletArc"),sQuery(id+"F0.wireOp",EDGE,"E25.0"),sQuery(id+"F0.wireOp",EDGE,"E25.1"),sQuery(id+"F0.wireOp",EDGE,"E25.2"),sQuery(id+"F0.wireOp",EDGE,"E25.3"),sQuery(id+"F0.wireOp",EDGE,"E25.4"),sQuery(id+"F0.wireOp",EDGE,"E25.5"),sQuery(id+"F0.wireOp",EDGE,"E25.6"),sQuery(id+"F0.wireOp",EDGE,"E25.7")])],"isStart":false});
            extrude(context, id + "F17", {"entities" : qUnion([Q0]), "endBound" : BoundingType.UP_TO_SURFACE, "endBoundEntityFace" : qUnion([Q1]), "depth" : 25 * mm});
        }
    });
